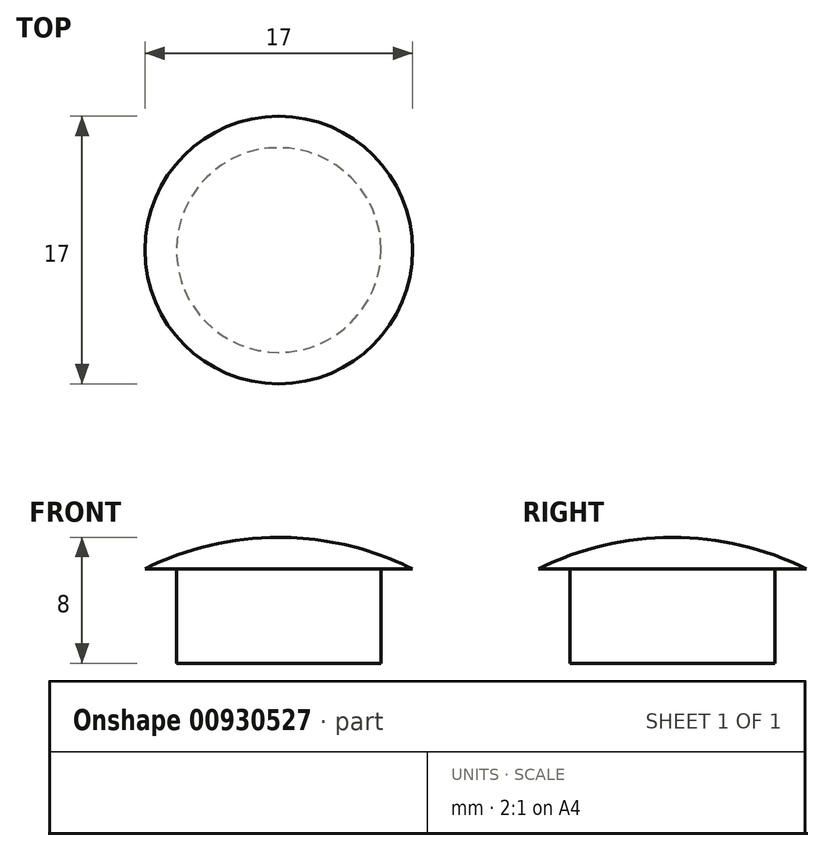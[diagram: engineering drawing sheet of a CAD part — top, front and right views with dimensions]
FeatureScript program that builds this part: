
annotation { "Feature Type Name" : "Feature", "Feature Type Description" : "" }
export const myFeature = defineFeature(function(context is Context, id is Id, definition is map)
    precondition{}
    {
        {
            var Q0;
            Q0=qCreatedBy(makeId("Front.planeOp"),FACE);
            var sketch = newSketch(context, id + "F0", { "sketchPlane" : qUnion([Q0])});
            skArc(sketch, "E0", {"start": v(8.5, 0) * mm, "mid": v(0, 2) * mm, "end": v(-8.5, 0) * mm});
            skLineSegment(sketch, "E1", {"start": v(-8.5, 0) * mm, "end": v(-6.5, 0) * mm});
            skLineSegment(sketch, "E2", {"start": v(-6.5, 0) * mm, "end": v(-6.5, -6) * mm});
            skLineSegment(sketch, "E3", {"start": v(-6.5, -6) * mm, "end": v(6.5, -6) * mm});
            skLineSegment(sketch, "E4.MirrorCS", {"start": v(6.5, 0) * mm, "end": v(6.5, -6) * mm});
            skPoint(sketch, "E5.orphan", {"position": v(6.5, -6) * mm});
            skLineSegment(sketch, "E6.trimOffspring", {"start": v(6.5, 0) * mm, "end": v(8.5, 0) * mm});
            skLineSegment(sketch, "E7", {"start": v(0, 2) * mm, "end": v(0, -6) * mm});
            skSolve(sketch);
        }
        {
            var Q0;
            {var subQ1=sQuery(id+"F0.wireOp",EDGE,"E4.MirrorCS");Q0=makeQuery(id+"F0.imprint","IMPRINT",FACE,{"disambiguationData":[TD([[makeQuery(id+"F0.imprint","IMPRINT",EDGE,{"derivedFrom":subQ1}),-1.0]])]});}
            var Q1;
            Q1=sQuery(id+"F0.wireOp",EDGE,"E7");
            revolve(context, id + "F1", {"surfaceOperationType" : NewSurfaceOperationType.NEW, "entities" : qUnion([Q0]), "axis" : qUnion([Q1]), "revolveType" : RevolveType.FULL});
        }
    });
